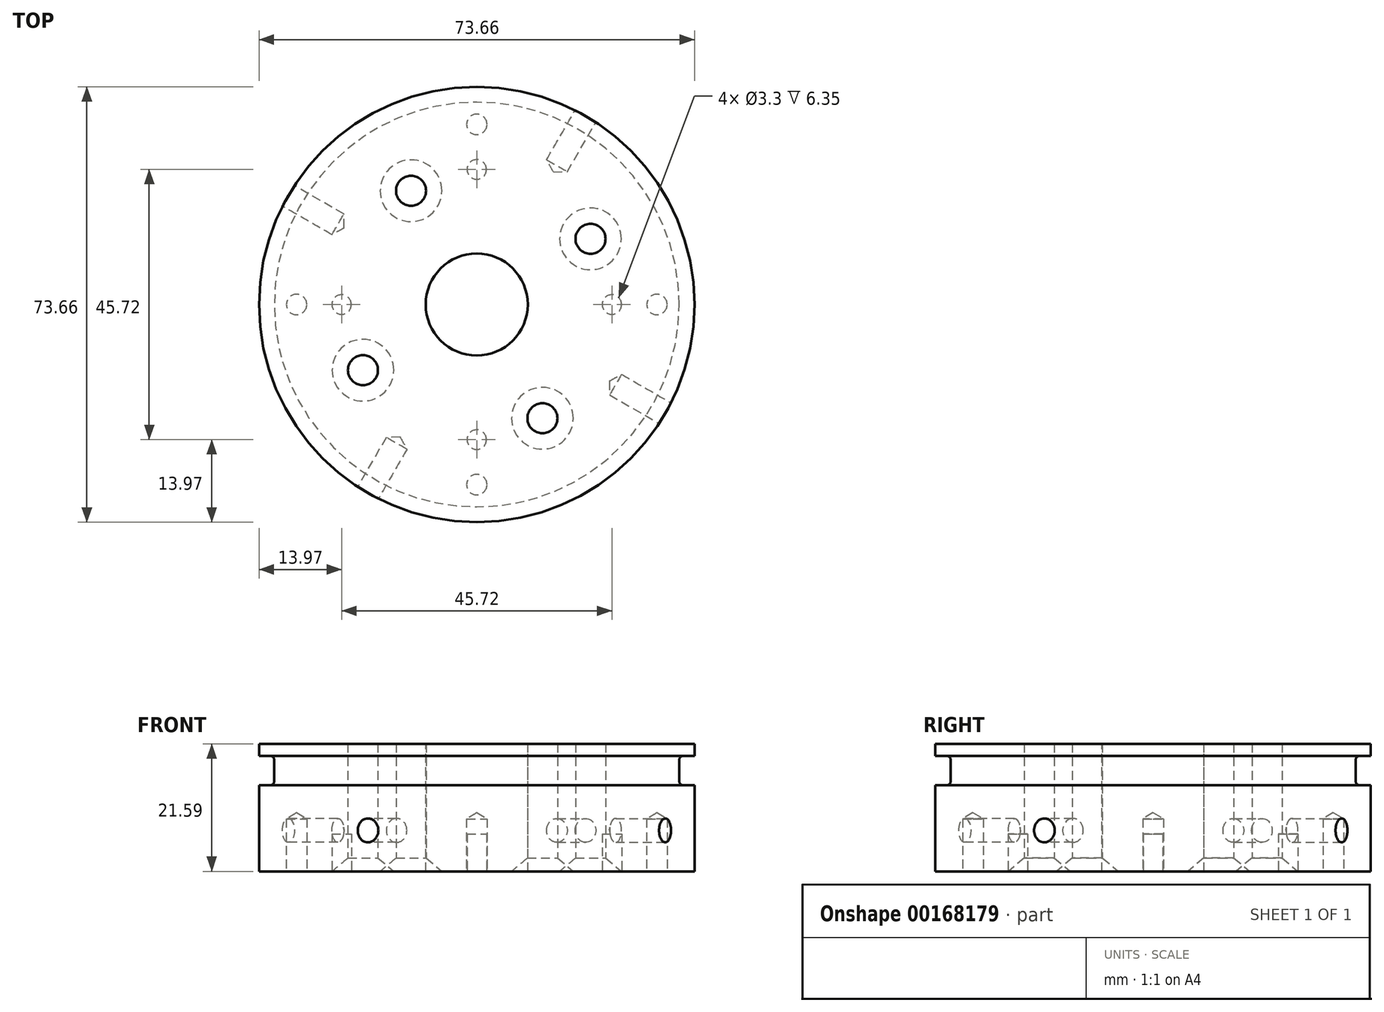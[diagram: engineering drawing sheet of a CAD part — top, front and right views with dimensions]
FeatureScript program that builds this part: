
annotation { "Feature Type Name" : "Feature", "Feature Type Description" : "" }
export const myFeature = defineFeature(function(context is Context, id is Id, definition is map)
    precondition{}
    {
        {
            var Q0;
            Q0=qCreatedBy(makeId("Top.planeOp"),FACE);
            var sketch = newSketch(context, id + "F0", { "sketchPlane" : qUnion([Q0])});
            skCircle(sketch, "E0", {"center": v(0, 0) * mm, "radius": 36.83 * mm});
            skSolve(sketch);
        }
        {
            var Q0;
            Q0=makeQuery(id+"F0.imprint","IMPRINT",FACE,{"disambiguationData":[TD([[makeQuery(id+"F0.imprint","IMPRINT",EDGE,{"derivedFrom":sQuery(id+"F0.wireOp",EDGE,"E0")}),1.0]])]});
            extrude(context, id + "F1", {"entities" : qUnion([Q0]), "depth" : 21.59 * mm});
        }
        {
            var Q0;
            Q0=makeQuery(id+"FNZgXB3MDCEPfWC_1.boolean.opBoolean","SPLIT",FACE,{"disambiguationData":[TD([makeQuery(id+"FNZgXB3MDCEPfWC_1.opExtrude","SWEPT_FACE",FACE,{"disambiguationData":[OSD([sQuery(id+"FiLk9hSRQ8Dv81E_1.wireOp",EDGE,"Xvq2NHEn-EDZK-GzOR-rNrk-moL4fFsD4KvI")])]})])],"derivedFrom":makeQuery(id+"F1.opExtrude","CAP_FACE",FACE,{"disambiguationData":[OSD([sQuery(id+"F0.wireOp",EDGE,"E0")])],"isStart":false})});
            var sketch = newSketch(context, id + "F2", { "sketchPlane" : qUnion([Q0])});
            skCircle(sketch, "E1", {"center": v(0, 0) * mm, "radius": 8.64 * mm});
            skSolve(sketch);
        }
        {
            var Q0;
            Q0=qSketchRegion(id+"F2",true);
            extrude(context, id + "F3", {"entities" : qUnion([Q0]), "operationType" : NewBodyOperationType.REMOVE, "endBound" : BoundingType.THROUGH_ALL, "oppositeDirection" : true, "depth" : 25.4 * mm});
        }
        {
            var Q0;
            Q0=makeQuery(id+"FOQC5dfjhO448EJ_1.boolean.opBoolean","SPLIT",FACE,{"disambiguationData":[TD([makeQuery(id+"F3.boolean.opBoolean","COPY",FACE,{"derivedFrom":makeQuery(id+"F3.opExtrude","SWEPT_FACE",FACE,{"disambiguationData":[OSD([sQuery(id+"F2.wireOp",EDGE,"E1")])]})})])],"derivedFrom":makeQuery(id+"F1.opExtrude","CAP_FACE",FACE,{"disambiguationData":[OSD([sQuery(id+"F0.wireOp",EDGE,"E0")])],"isStart":false})});
            cPlane(context, id + "F4", {"entities" : qUnion([Q0]), "cplaneType" : CPlaneType.OFFSET, "offset" : 2.03 * mm, "oppositeDirection" : true, "width" : 152.4 * mm, "height" : 152.4 * mm});
        }
        {
            var Q0;
            Q0=qCreatedBy(id+"F4.planeOp",FACE);
            var sketch = newSketch(context, id + "F5", { "sketchPlane" : qUnion([Q0])});
            skCircle(sketch, "E2", {"center": v(0, 0) * mm, "radius": 34.24 * mm});
            skCircle(sketch, "E3.0", {"center": v(0, 0) * mm, "radius": 36.83 * mm});
            skSolve(sketch);
        }
        {
            var Q0;
            Q0 = qSketchRegion(id + "F5", true);
            extrude(context, id + "F6", {"entities" : qUnion([Q0]), "operationType" : NewBodyOperationType.REMOVE, "oppositeDirection" : true, "depth" : 5 * mm});
        }
        {
            var Q0;
            Q0=makeQuery(id+"F6.boolean.opBoolean","COPY",EDGE,{"derivedFrom":makeQuery(id+"F6.opExtrude","CAP_EDGE",EDGE,{"disambiguationData":[OSD([sQuery(id+"F5.wireOp",EDGE,"E2")])],"isStart":false})});
            var Q1;
            Q1=makeQuery(id+"F6.boolean.opBoolean","COPY",EDGE,{"derivedFrom":makeQuery(id+"F6.opExtrude","CAP_EDGE",EDGE,{"disambiguationData":[OSD([sQuery(id+"F5.wireOp",EDGE,"E2")])],"isStart":true})});
            fillet(context, id + "F7", {"entities" : qUnion([Q0, Q1]), "radius" : 0.76 * mm, "tangentPropagation" : true, "allowEdgeOverflow" : false});
        }
        {
            var Q0;
            {var subQ1=sQuery(id+"F0.wireOp",EDGE,"E0");var subQ2=makeQuery(id+"F1.opExtrude","SWEPT_FACE",FACE,{"disambiguationData":[OSD([subQ1])]});Q0=makeQuery(id+"FkcieFRIapZdHPD_1.boolean.opBoolean","SPLIT",FACE,{"disambiguationData":[TD([subQ2])],"derivedFrom":makeQuery(id+"F1.opExtrude","CAP_FACE",FACE,{"disambiguationData":[OSD([subQ1])],"isStart":false})});}
            var sketch = newSketch(context, id + "F8", { "sketchPlane" : qUnion([Q0])});
            skCircle(sketch, "E4.0", {"center": v(0, 0) * mm, "radius": 36.83 * mm, "construction": true});
            skPoint(sketch, "E5", {"position": v(-18.41, -31.9) * mm});
            skLineSegment(sketch, "E6", {"start": v(0, -36.83) * mm, "end": v(0, 0) * mm, "construction": true});
            skLineSegment(sketch, "E7", {"start": v(0, 0) * mm, "end": v(-17.96, -31.1) * mm, "construction": true});
            skLineSegment(sketch, "E8", {"start": v(-17.96, -31.1) * mm, "end": v(-18.41, -31.9) * mm, "construction": true});
            skLineSegment(sketch, "E9", {"start": v(0, 0) * mm, "end": v(18.41, 31.9) * mm, "construction": true});
            skLineSegment(sketch, "E10", {"start": v(18.41, 31.9) * mm, "end": v(0, 0) * mm, "construction": true});
            skLineSegment(sketch, "E11", {"start": v(31.9, -18.41) * mm, "end": v(0, 0) * mm, "construction": true});
            skLineSegment(sketch, "E12", {"start": v(0, 0) * mm, "end": v(-31.9, 18.41) * mm, "construction": true});
            skPoint(sketch, "E13", {"position": v(18.41, 31.9) * mm});
            skPoint(sketch, "E14", {"position": v(31.9, -18.41) * mm});
            skPoint(sketch, "E15", {"position": v(-31.9, 18.41) * mm});
            skSolve(sketch);
        }
        {
            var Q0;
            Q0=qCreatedBy(makeId("Front.planeOp"),FACE);
            var sketch = newSketch(context, id + "F9", { "sketchPlane" : qUnion([Q0])});
            skLineSegment(sketch, "E16", {"start": v(0, 0) * mm, "end": v(0, 38.57) * mm, "construction": true});
            skSolve(sketch);
        }
        {
            var Q0;
            Q0=sQuery(id+"F9.wireOp",EDGE,"E16");
            cPlane(context, id + "F10", {"entities" : qUnion([Q0]), "cplaneType" : CPlaneType.LINE_ANGLE, "offset" : 25.4 * mm, "angle" : 60 * degree, "width" : 152.4 * mm, "height" : 152.4 * mm});
        }
        {
            var Q0;
            Q0=sQuery(id+"F8.wireOp",VERTEX,"E5");
            var Q1;
            Q1=qCreatedBy(id+"F10.planeOp",FACE);
            cPlane(context, id + "F11", {"entities" : qUnion([Q0, Q1]), "cplaneType" : CPlaneType.PLANE_POINT, "offset" : 25.4 * mm, "width" : 152.4 * mm, "height" : 152.4 * mm});
        }
        {
            var Q0;
            Q0=qCreatedBy(id+"F11.planeOp",FACE);
            var Q1;
            Q1=sQuery(id+"F8.wireOp",VERTEX,"E13");
            cPlane(context, id + "F12", {"entities" : qUnion([Q0, Q1]), "cplaneType" : CPlaneType.PLANE_POINT, "offset" : 25.4 * mm, "width" : 152.4 * mm, "height" : 152.4 * mm});
        }
        {
            var Q0;
            Q0=sQuery(id+"F9.wireOp",EDGE,"E16");
            cPlane(context, id + "F13", {"entities" : qUnion([Q0]), "cplaneType" : CPlaneType.LINE_ANGLE, "offset" : 25.4 * mm, "angle" : 150 * degree, "width" : 152.4 * mm, "height" : 152.4 * mm});
        }
        {
            var Q0;
            Q0=sQuery(id+"F8.wireOp",VERTEX,"E15");
            var Q1;
            Q1=qCreatedBy(id+"F13.planeOp",FACE);
            cPlane(context, id + "F14", {"entities" : qUnion([Q0, Q1]), "cplaneType" : CPlaneType.PLANE_POINT, "offset" : 25.4 * mm, "width" : 152.4 * mm, "height" : 152.4 * mm});
        }
        {
            var Q0;
            Q0=qCreatedBy(id+"F13.planeOp",FACE);
            var Q1;
            Q1=sQuery(id+"F8.wireOp",VERTEX,"E14");
            cPlane(context, id + "F15", {"entities" : qUnion([Q0, Q1]), "cplaneType" : CPlaneType.PLANE_POINT, "offset" : 25.4 * mm, "width" : 152.4 * mm, "height" : 152.4 * mm});
        }
        {
            var Q0;
            Q0=qCreatedBy(id+"F11.planeOp",FACE);
            var sketch = newSketch(context, id + "F16", { "sketchPlane" : qUnion([Q0])});
            skLineSegment(sketch, "E17", {"start": v(0, 0) * mm, "end": v(0, 6.93) * mm, "construction": true});
            skPoint(sketch, "E18", {"position": v(0, 6.93) * mm});
            skSolve(sketch);
        }
        {
            var Q0;
            Q0=qCreatedBy(id+"F12.planeOp",FACE);
            var sketch = newSketch(context, id + "F17", { "sketchPlane" : qUnion([Q0])});
            skPoint(sketch, "E19", {"position": v(0, 6.93) * mm});
            skLineSegment(sketch, "E20.0", {"start": v(0, 0) * mm, "end": v(0, 6.93) * mm, "construction": true});
            skSolve(sketch);
        }
        {
            var Q0;
            Q0=qCreatedBy(id+"F14.planeOp",FACE);
            var sketch = newSketch(context, id + "F18", { "sketchPlane" : qUnion([Q0])});
            skLineSegment(sketch, "E21", {"start": v(0, 0) * mm, "end": v(0, 6.93) * mm, "construction": true});
            skLineSegment(sketch, "E22.0", {"start": v(-36.83, 0) * mm, "end": v(-36.83, 6.93) * mm, "construction": true});
            skPoint(sketch, "E23", {"position": v(0, 6.93) * mm});
            skLineSegment(sketch, "E24", {"start": v(-36.83, 6.93) * mm, "end": v(0, 6.93) * mm, "construction": true});
            skSolve(sketch);
        }
        {
            var Q0;
            Q0=qCreatedBy(id+"F15.planeOp",FACE);
            var sketch = newSketch(context, id + "F19", { "sketchPlane" : qUnion([Q0])});
            skLineSegment(sketch, "E25.0", {"start": v(0, 0) * mm, "end": v(0, 6.93) * mm, "construction": true});
            skPoint(sketch, "E26", {"position": v(0, 6.93) * mm});
            skSolve(sketch);
        }
        {
            var Q0;
            Q0=sQuery(id+"F19.wireOp",VERTEX,"E26");
            var Q1;
            Q1=makeQuery(id+"F1.opExtrude","SWEPT_BODY",BODY,{"disambiguationData":[OSD([sQuery(id+"F0.wireOp",EDGE,"E0")])]});
            hole(context, id + "F20", {"style" : HoleStyle.SIMPLE, "endStyle" : HoleEndStyle.BLIND, "oppositeDirection" : true, "standardTappedOrClearance" : lookupTablePath({ "standard" : "ANSI", "engagement" : "75%", "pitch" : "32 tpi", "size" : "#10", "type" : "Tapped" }), "standardBlindInLast" : lookupTablePath({ "standard" : "ANSI", "engagement" : "75%", "pitch" : "32 tpi", "size" : "#10", "type" : "Tapped" }), "holeDiameter" : 4.04 * mm, "holeDepth" : 9.65 * mm, "locations" : qUnion([Q0]), "scope" : qUnion([Q1]), "majorDiameter" : 4.83 * mm});
        }
        {
            var Q0;
            Q0=sQuery(id+"F18.wireOp",VERTEX,"E23");
            var Q1;
            Q1=makeQuery(id+"F1.opExtrude","SWEPT_BODY",BODY,{"disambiguationData":[OSD([sQuery(id+"F0.wireOp",EDGE,"E0")])]});
            hole(context, id + "F21", {"style" : HoleStyle.SIMPLE, "endStyle" : HoleEndStyle.BLIND, "standardTappedOrClearance" : lookupTablePath({ "standard" : "ANSI", "engagement" : "75%", "pitch" : "32 tpi", "size" : "#10", "type" : "Tapped" }), "standardBlindInLast" : lookupTablePath({ "standard" : "ANSI", "engagement" : "75%", "pitch" : "32 tpi", "size" : "#10", "type" : "Tapped" }), "holeDiameter" : 4.04 * mm, "holeDepth" : 9.65 * mm, "locations" : qUnion([Q0]), "scope" : qUnion([Q1]), "majorDiameter" : 4.83 * mm});
        }
        {
            var Q0;
            Q0=sQuery(id+"F16.wireOp",VERTEX,"E18");
            var Q1;
            Q1=makeQuery(id+"F1.opExtrude","SWEPT_BODY",BODY,{"disambiguationData":[OSD([sQuery(id+"F0.wireOp",EDGE,"E0")])]});
            hole(context, id + "F22", {"style" : HoleStyle.SIMPLE, "endStyle" : HoleEndStyle.BLIND, "oppositeDirection" : true, "standardTappedOrClearance" : lookupTablePath({ "standard" : "ANSI", "engagement" : "75%", "pitch" : "32 tpi", "size" : "#10", "type" : "Tapped" }), "standardBlindInLast" : lookupTablePath({ "standard" : "ANSI", "engagement" : "75%", "pitch" : "32 tpi", "size" : "#10", "type" : "Tapped" }), "holeDiameter" : 4.04 * mm, "holeDepth" : 9.65 * mm, "locations" : qUnion([Q0]), "scope" : qUnion([Q1]), "majorDiameter" : 4.83 * mm});
        }
        {
            var Q0;
            Q0=sQuery(id+"F17.wireOp",VERTEX,"E19");
            var Q1;
            Q1=makeQuery(id+"F1.opExtrude","SWEPT_BODY",BODY,{"disambiguationData":[OSD([sQuery(id+"F0.wireOp",EDGE,"E0")])]});
            hole(context, id + "F23", {"style" : HoleStyle.SIMPLE, "endStyle" : HoleEndStyle.BLIND, "standardTappedOrClearance" : lookupTablePath({ "standard" : "ANSI", "engagement" : "75%", "pitch" : "32 tpi", "size" : "#10", "type" : "Tapped" }), "standardBlindInLast" : lookupTablePath({ "standard" : "ANSI", "engagement" : "75%", "pitch" : "32 tpi", "size" : "#10", "type" : "Tapped" }), "holeDiameter" : 4.04 * mm, "holeDepth" : 9.65 * mm, "locations" : qUnion([Q0]), "scope" : qUnion([Q1]), "majorDiameter" : 4.83 * mm});
        }
        {
            var Q0;
            Q0=makeQuery(id+"F1.opExtrude","CAP_FACE",FACE,{"disambiguationData":[OSD([sQuery(id+"F0.wireOp",EDGE,"E0")])],"isStart":true});
            var sketch = newSketch(context, id + "F24", { "sketchPlane" : qUnion([Q0])});
            skLineSegment(sketch, "E27", {"start": v(0, 0) * mm, "end": v(-11.11, -19.25) * mm, "construction": true});
            skPoint(sketch, "E28", {"position": v(-11.11, -19.25) * mm});
            skPoint(sketch, "E29.1.0", {"position": v(19.25, -11.11) * mm});
            skPoint(sketch, "E29.2.0", {"position": v(11.11, 19.25) * mm});
            skPoint(sketch, "E29.3.0", {"position": v(-19.25, 11.11) * mm});
            skPoint(sketch, "E29.center", {"position": v(0, 0) * mm});
            skSolve(sketch);
        }
        {
            var Q0;
            Q0=sQuery(id+"F24.wireOp",VERTEX,"E29.3.0");
            var Q1;
            Q1=sQuery(id+"F24.wireOp",VERTEX,"E28");
            var Q2;
            Q2=sQuery(id+"F24.wireOp",VERTEX,"E29.1.0");
            var Q3;
            Q3=sQuery(id+"F24.wireOp",VERTEX,"E29.2.0");
            var Q4;
            Q4=makeQuery(id+"F1.opExtrude","SWEPT_BODY",BODY,{"disambiguationData":[OSD([sQuery(id+"F0.wireOp",EDGE,"E0")])]});
            hole(context, id + "F25", {"style" : HoleStyle.C_SINK, "endStyle" : HoleEndStyle.THROUGH, "holeDiameter" : 5.08 * mm, "cSinkDiameter" : 10.44 * mm, "cSinkAngle" : 100 * degree, "locations" : qUnion([Q0, Q1, Q2, Q3]), "scope" : qUnion([Q4]), "isTappedThrough" : true});
        }
        {
            var Q0;
            Q0=makeQuery(id+"F1.opExtrude","CAP_FACE",FACE,{"disambiguationData":[OSD([sQuery(id+"F0.wireOp",EDGE,"E0")])],"isStart":true});
            var sketch = newSketch(context, id + "F26", { "sketchPlane" : qUnion([Q0])});
            skPoint(sketch, "E30", {"position": v(-30.48, 0) * mm});
            skPoint(sketch, "E31.1.0", {"position": v(0, -30.48) * mm});
            skPoint(sketch, "E31.2.0", {"position": v(30.48, 0) * mm});
            skPoint(sketch, "E31.3.0", {"position": v(0, 30.48) * mm});
            skPoint(sketch, "E31.center", {"position": v(0, 0) * mm});
            skSolve(sketch);
        }
        {
            var Q0;
            Q0=sQuery(id+"F26.wireOp",VERTEX,"E30");
            var Q1;
            Q1=sQuery(id+"F26.wireOp",VERTEX,"E31.1.0");
            var Q2;
            Q2=sQuery(id+"F26.wireOp",VERTEX,"E31.3.0");
            var Q3;
            Q3=sQuery(id+"F26.wireOp",VERTEX,"E31.2.0");
            var Q4;
            Q4=makeQuery(id+"F1.opExtrude","SWEPT_BODY",BODY,{"disambiguationData":[OSD([sQuery(id+"F0.wireOp",EDGE,"E0")])]});
            hole(context, id + "F27", {"style" : HoleStyle.SIMPLE, "endStyle" : HoleEndStyle.BLIND, "standardTappedOrClearance" : lookupTablePath({ "standard" : "ANSI", "engagement" : "75%", "pitch" : "32 tpi", "size" : "#8", "type" : "Tapped" }), "standardBlindInLast" : lookupTablePath({ "standard" : "ANSI", "engagement" : "75%", "pitch" : "32 tpi", "size" : "#8", "type" : "Tapped" }), "holeDiameter" : 3.45 * mm, "holeDepth" : 8.9 * mm, "locations" : qUnion([Q0, Q1, Q2, Q3]), "scope" : qUnion([Q4]), "majorDiameter" : 4.17 * mm});
        }
        {
            var Q0;
            Q0=makeQuery(id+"F1.opExtrude","CAP_FACE",FACE,{"disambiguationData":[OSD([sQuery(id+"F0.wireOp",EDGE,"E0")])],"isStart":true});
            var sketch = newSketch(context, id + "F28", { "sketchPlane" : qUnion([Q0])});
            skCircle(sketch, "E32", {"center": v(-22.86, 0) * mm, "radius": 1.65 * mm});
            skCircle(sketch, "E33.1.0", {"center": v(0, -22.86) * mm, "radius": 1.65 * mm});
            skCircle(sketch, "E33.2.0", {"center": v(22.86, 0) * mm, "radius": 1.65 * mm});
            skCircle(sketch, "E33.3.0", {"center": v(0, 22.86) * mm, "radius": 1.65 * mm});
            skPoint(sketch, "E33.center", {"position": v(0, 0) * mm});
            skSolve(sketch);
        }
        {
            var Q0;
            Q0 = qSketchRegion(id + "F28", true);
            extrude(context, id + "F29", {"entities" : qUnion([Q0]), "operationType" : NewBodyOperationType.REMOVE, "oppositeDirection" : true, "depth" : 6.35 * mm});
        }
    });
